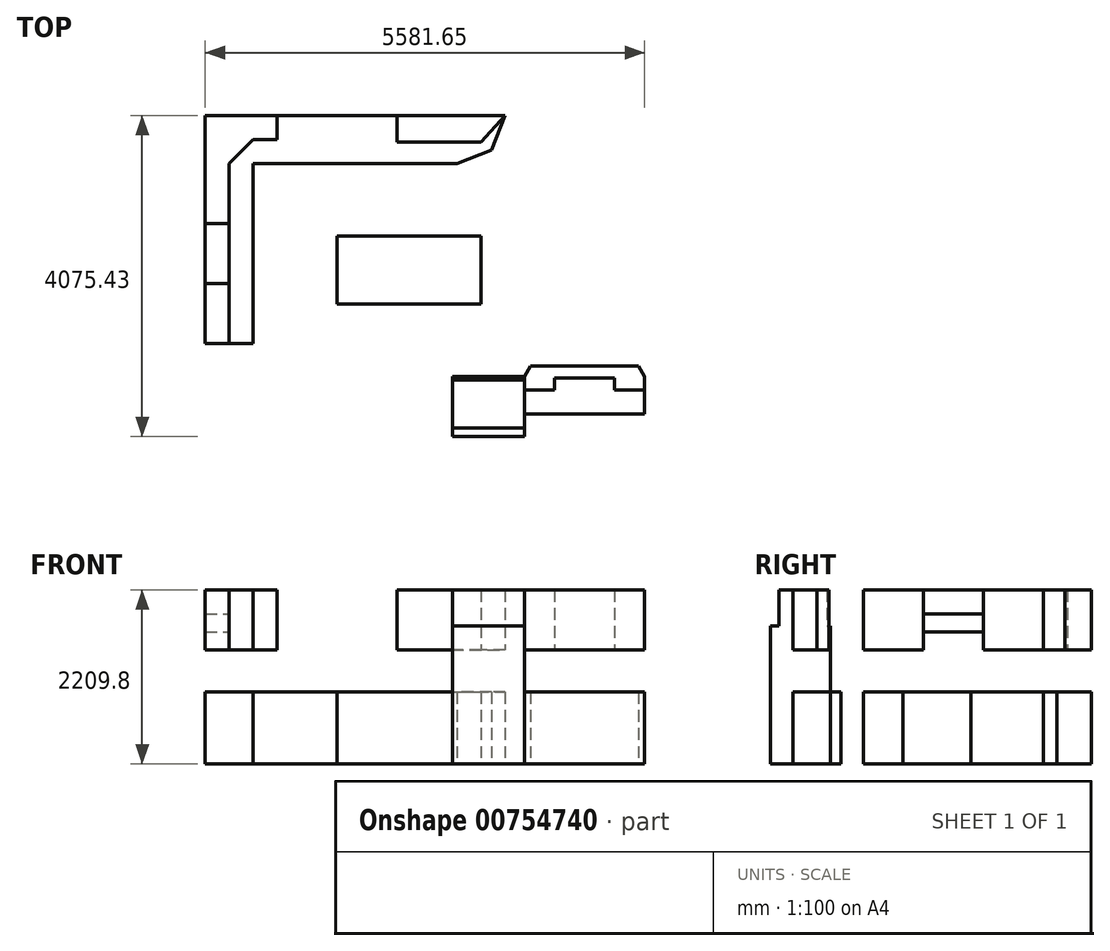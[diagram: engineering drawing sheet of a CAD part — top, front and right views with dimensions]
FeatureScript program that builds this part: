
annotation { "Feature Type Name" : "Feature", "Feature Type Description" : "" }
export const myFeature = defineFeature(function(context is Context, id is Id, definition is map)
    precondition{}
    {
        {
            var Q0;
            Q0=qCreatedBy(makeId("Top.planeOp"),FACE);
            cPlane(context, id + "F0", {"entities" : qUnion([Q0]), "cplaneType" : CPlaneType.OFFSET, "offset" : 1447.8 * mm, "width" : 152.4 * mm, "height" : 152.4 * mm});
        }
        {
            var Q0;
            Q0=qCreatedBy(makeId("Top.planeOp"),FACE);
            cPlane(context, id + "F1", {"entities" : qUnion([Q0]), "cplaneType" : CPlaneType.OFFSET, "offset" : 2286 * mm, "width" : 152.4 * mm, "height" : 152.4 * mm});
        }
        {
            var Q0;
            Q0=qCreatedBy(makeId("Top.planeOp"),FACE);
            var sketch = newSketch(context, id + "F2", { "sketchPlane" : qUnion([Q0])});
            skLineSegment(sketch, "E0", {"start": v(0, 0) * mm, "end": v(1009.65, 0) * mm});
            skLineSegment(sketch, "E1", {"start": v(1009.65, 0) * mm, "end": v(2343.15, 0) * mm, "construction": true});
            skLineSegment(sketch, "E2", {"start": v(2343.15, 0) * mm, "end": v(4025.9, 0) * mm});
            skLineSegment(sketch, "E3", {"start": v(4025.9, 0) * mm, "end": v(5886.45, 0) * mm, "construction": true});
            skLineSegment(sketch, "E4", {"start": v(5886.45, 0) * mm, "end": v(6648.45, 0) * mm});
            skLineSegment(sketch, "E5", {"start": v(6648.45, 0) * mm, "end": v(6648.45, -247.65) * mm});
            skLineSegment(sketch, "E6", {"start": v(6648.45, -247.65) * mm, "end": v(6648.45, -1917.7) * mm, "construction": true});
            skLineSegment(sketch, "E7", {"start": v(6648.45, -2889.25) * mm, "end": v(6648.45, -3790.95) * mm});
            skLineSegment(sketch, "E8", {"start": v(6648.45, -3790.95) * mm, "end": v(5734.05, -3790.95) * mm, "construction": true});
            skLineSegment(sketch, "E9", {"start": v(5734.05, -3790.95) * mm, "end": v(4019.55, -3790.95) * mm});
            skLineSegment(sketch, "E10", {"start": v(3028.95, -3790.95) * mm, "end": v(3028.95, -4095.75) * mm});
            skLineSegment(sketch, "E11", {"start": v(3028.95, -4095.75) * mm, "end": v(1784.35, -4095.75) * mm, "construction": true});
            skLineSegment(sketch, "E12", {"start": v(1784.35, -4095.75) * mm, "end": v(920.75, -4095.75) * mm});
            skLineSegment(sketch, "E13", {"start": v(920.75, -4095.75) * mm, "end": v(0, -4095.75) * mm, "construction": true});
            skLineSegment(sketch, "E14", {"start": v(0, -4095.75) * mm, "end": v(0, -3048) * mm, "construction": true});
            skLineSegment(sketch, "E15", {"start": v(0, -3048) * mm, "end": v(0, -2895.6) * mm});
            skLineSegment(sketch, "E16", {"start": v(0, -2895.6) * mm, "end": v(0, 0) * mm});
            skLineSegment(sketch, "E17", {"start": v(6648.45, -1917.7) * mm, "end": v(6648.45, -2889.25) * mm, "construction": true});
            skLineSegment(sketch, "E18", {"start": v(3943.35, -3905.25) * mm, "end": v(4057.65, -3905.25) * mm});
            skLineSegment(sketch, "E19", {"start": v(4057.65, -3905.25) * mm, "end": v(4057.65, -4184.65) * mm});
            skLineSegment(sketch, "E20", {"start": v(4057.65, -4184.65) * mm, "end": v(3143.25, -4184.65) * mm});
            skLineSegment(sketch, "E21", {"start": v(3143.25, -4184.65) * mm, "end": v(3143.25, -3905.25) * mm});
            skLineSegment(sketch, "E22", {"start": v(3143.25, -3905.25) * mm, "end": v(3257.55, -3905.25) * mm});
            skLineSegment(sketch, "E23", {"start": v(3257.55, -3905.25) * mm, "end": v(3257.55, -3790.95) * mm});
            skLineSegment(sketch, "E24", {"start": v(3257.55, -3790.95) * mm, "end": v(3028.95, -3790.95) * mm});
            skLineSegment(sketch, "E25", {"start": v(3943.35, -3905.25) * mm, "end": v(3943.35, -3790.95) * mm});
            skLineSegment(sketch, "E26", {"start": v(3943.35, -3790.95) * mm, "end": v(4019.55, -3790.95) * mm});
            skPoint(sketch, "E27", {"position": v(3143.25, -3790.95) * mm});
            skPoint(sketch, "E28", {"position": v(4057.65, -3790.95) * mm});
            skSolve(sketch);
        }
        {
            var Q0;
            Q0=qCreatedBy(makeId("Top.planeOp"),FACE);
            var sketch = newSketch(context, id + "F3", { "sketchPlane" : qUnion([Q0])});
            skLineSegment(sketch, "E29.bottom", {"start": v(0, -2895.6) * mm, "end": v(609.6, -2895.6) * mm});
            skLineSegment(sketch, "E29.top", {"start": v(0, -2133.6) * mm, "end": v(609.6, -2133.6) * mm});
            skLineSegment(sketch, "E29.left", {"start": v(0, -2895.6) * mm, "end": v(0, -2133.6) * mm});
            skLineSegment(sketch, "E29.right", {"start": v(609.6, -2895.6) * mm, "end": v(609.6, -2133.6) * mm});
            skLineSegment(sketch, "E30.top", {"start": v(0, -1371.6) * mm, "end": v(609.6, -1371.6) * mm});
            skLineSegment(sketch, "E30.left", {"start": v(0, -2133.6) * mm, "end": v(0, -1371.6) * mm});
            skLineSegment(sketch, "E30.right", {"start": v(609.6, -2133.6) * mm, "end": v(609.6, -1371.6) * mm});
            skLineSegment(sketch, "E31.top", {"start": v(0, -914.4) * mm, "end": v(609.6, -914.4) * mm});
            skLineSegment(sketch, "E31.left", {"start": v(0, -1371.6) * mm, "end": v(0, -914.4) * mm});
            skLineSegment(sketch, "E31.right", {"start": v(609.6, -1371.6) * mm, "end": v(609.6, -914.4) * mm});
            skLineSegment(sketch, "E32", {"start": v(609.6, -914.4) * mm, "end": v(609.6, -609.6) * mm});
            skLineSegment(sketch, "E33", {"start": v(609.6, -609.6) * mm, "end": v(914.4, -609.6) * mm});
            skLineSegment(sketch, "E34", {"start": v(914.4, -609.6) * mm, "end": v(914.4, 0) * mm});
            skLineSegment(sketch, "E35", {"start": v(914.4, 0) * mm, "end": v(0, 0) * mm});
            skLineSegment(sketch, "E36", {"start": v(0, 0) * mm, "end": v(0, -914.4) * mm});
            skLineSegment(sketch, "E37.bottom", {"start": v(1219.2, -609.6) * mm, "end": v(2133.6, -609.6) * mm});
            skLineSegment(sketch, "E37.top", {"start": v(1219.2, 0) * mm, "end": v(2133.6, 0) * mm});
            skLineSegment(sketch, "E37.left", {"start": v(1219.2, -609.6) * mm, "end": v(1219.2, 0) * mm});
            skLineSegment(sketch, "E37.right", {"start": v(2133.6, -609.6) * mm, "end": v(2133.6, 0) * mm});
            skPoint(sketch, "E38", {"position": v(1676.4, -609.6) * mm});
            skLineSegment(sketch, "E39.bottom", {"start": v(914.4, -609.6) * mm, "end": v(1219.2, -609.6) * mm});
            skLineSegment(sketch, "E39.top", {"start": v(914.4, 0) * mm, "end": v(1219.2, 0) * mm});
            skLineSegment(sketch, "E40.bottom", {"start": v(2133.6, -609.6) * mm, "end": v(2743.2, -609.6) * mm});
            skLineSegment(sketch, "E40.top", {"start": v(2133.6, 0) * mm, "end": v(2743.2, 0) * mm});
            skLineSegment(sketch, "E40.right", {"start": v(2743.2, -609.6) * mm, "end": v(2743.2, 0) * mm});
            skLineSegment(sketch, "E41.bottom", {"start": v(2743.2, -609.6) * mm, "end": v(3200.4, -609.6) * mm});
            skLineSegment(sketch, "E41.top", {"start": v(2743.2, 0) * mm, "end": v(3200.4, 0) * mm});
            skLineSegment(sketch, "E41.right", {"start": v(3200.4, -609.6) * mm, "end": v(3200.4, 0) * mm});
            skLineSegment(sketch, "E42", {"start": v(3200.4, 0) * mm, "end": v(3810, 0) * mm});
            skLineSegment(sketch, "E43", {"start": v(3810, 0) * mm, "end": v(3637.62, -437.22) * mm});
            skLineSegment(sketch, "E44", {"start": v(3637.62, -437.22) * mm, "end": v(3200.4, -609.6) * mm});
            skSolve(sketch);
        }
        {
            var Q0;
            Q0=qCreatedBy(id+"F0.planeOp",FACE);
            var sketch = newSketch(context, id + "F4", { "sketchPlane" : qUnion([Q0])});
            skLineSegment(sketch, "E45.bottom", {"start": v(0, -2895.6) * mm, "end": v(304.8, -2895.6) * mm});
            skLineSegment(sketch, "E45.top", {"start": v(0, -2133.6) * mm, "end": v(304.8, -2133.6) * mm});
            skLineSegment(sketch, "E45.left", {"start": v(0, -2895.6) * mm, "end": v(0, -2133.6) * mm});
            skLineSegment(sketch, "E45.right", {"start": v(304.8, -2895.6) * mm, "end": v(304.8, -2133.6) * mm});
            skLineSegment(sketch, "E46.top", {"start": v(0, -1371.6) * mm, "end": v(304.8, -1371.6) * mm});
            skLineSegment(sketch, "E47.top", {"start": v(0, -609.6) * mm, "end": v(304.8, -609.6) * mm});
            skLineSegment(sketch, "E47.left", {"start": v(0, -1371.6) * mm, "end": v(0, -609.6) * mm});
            skLineSegment(sketch, "E47.right", {"start": v(304.8, -1371.6) * mm, "end": v(304.8, -609.6) * mm});
            skLineSegment(sketch, "E48", {"start": v(0, -609.6) * mm, "end": v(0, 0) * mm});
            skLineSegment(sketch, "E49", {"start": v(0, 0) * mm, "end": v(609.6, 0) * mm});
            skLineSegment(sketch, "E50", {"start": v(609.6, 0) * mm, "end": v(609.6, -304.8) * mm});
            skLineSegment(sketch, "E51", {"start": v(609.6, -304.8) * mm, "end": v(304.8, -609.6) * mm});
            skLineSegment(sketch, "E52.bottom", {"start": v(609.6, 0) * mm, "end": v(914.4, 0) * mm});
            skLineSegment(sketch, "E52.top", {"start": v(609.6, -304.8) * mm, "end": v(914.4, -304.8) * mm});
            skLineSegment(sketch, "E52.right", {"start": v(914.4, 0) * mm, "end": v(914.4, -304.8) * mm});
            skLineSegment(sketch, "E53", {"start": v(3810, 0) * mm, "end": v(3505.2, -336.01) * mm});
            skLineSegment(sketch, "E54", {"start": v(3505.2, -336.01) * mm, "end": v(3505.2, 0) * mm});
            skLineSegment(sketch, "E55", {"start": v(3505.2, 0) * mm, "end": v(3810, 0) * mm});
            skLineSegment(sketch, "E56.bottom", {"start": v(3505.2, 0) * mm, "end": v(2743.2, 0) * mm});
            skLineSegment(sketch, "E56.top", {"start": v(3505.2, -339.07) * mm, "end": v(2743.2, -339.07) * mm});
            skLineSegment(sketch, "E56.left", {"start": v(3505.2, 0) * mm, "end": v(3505.2, -339.07) * mm});
            skLineSegment(sketch, "E56.right", {"start": v(2743.2, 0) * mm, "end": v(2743.2, -339.07) * mm});
            skLineSegment(sketch, "E57.bottom", {"start": v(2743.2, 0) * mm, "end": v(2438.4, 0) * mm});
            skLineSegment(sketch, "E57.top", {"start": v(2743.2, -339.07) * mm, "end": v(2438.4, -339.07) * mm});
            skLineSegment(sketch, "E57.right", {"start": v(2438.4, 0) * mm, "end": v(2438.4, -339.07) * mm});
            skSolve(sketch);
        }
        {
            var Q0;
            Q0=qCreatedBy(makeId("Top.planeOp"),FACE);
            var sketch = newSketch(context, id + "F5", { "sketchPlane" : qUnion([Q0])});
            skLineSegment(sketch, "E58.right", {"start": v(4057.65, -3313.33) * mm, "end": v(4057.65, -4075.33) * mm});
            skLineSegment(sketch, "E59.bottom", {"start": v(4133.85, -3790.95) * mm, "end": v(4819.65, -3790.95) * mm});
            skLineSegment(sketch, "E59.top", {"start": v(4133.85, -3181.35) * mm, "end": v(4819.65, -3181.35) * mm});
            skLineSegment(sketch, "E59.left", {"start": v(4133.85, -3790.95) * mm, "end": v(4133.85, -3181.35) * mm});
            skLineSegment(sketch, "E59.right", {"start": v(4819.65, -3790.95) * mm, "end": v(4819.65, -3181.35) * mm});
            skLineSegment(sketch, "E60.bottom", {"start": v(4819.65, -3181.35) * mm, "end": v(5505.45, -3181.35) * mm});
            skLineSegment(sketch, "E60.top", {"start": v(4819.65, -3790.95) * mm, "end": v(5505.45, -3790.95) * mm});
            skLineSegment(sketch, "E60.left", {"start": v(4819.65, -3181.35) * mm, "end": v(4819.65, -3790.95) * mm});
            skLineSegment(sketch, "E60.right", {"start": v(5505.45, -3181.35) * mm, "end": v(5505.45, -3790.95) * mm});
            skLineSegment(sketch, "E61", {"start": v(4133.85, -3181.35) * mm, "end": v(4057.65, -3313.33) * mm});
            skLineSegment(sketch, "E62", {"start": v(5505.45, -3181.35) * mm, "end": v(5581.65, -3313.33) * mm});
            skLineSegment(sketch, "E63", {"start": v(5581.65, -3313.33) * mm, "end": v(5581.65, -3790.95) * mm});
            skLineSegment(sketch, "E64", {"start": v(5581.65, -3790.95) * mm, "end": v(5505.45, -3790.95) * mm});
            skLineSegment(sketch, "E65", {"start": v(4133.85, -3790.95) * mm, "end": v(4057.65, -3790.95) * mm});
            skSolve(sketch);
        }
        {
            var Q0;
            Q0=qCreatedBy(id+"F0.planeOp",FACE);
            var sketch = newSketch(context, id + "F6", { "sketchPlane" : qUnion([Q0])});
            skLineSegment(sketch, "E66.bottom", {"start": v(4057.65, -3788.76) * mm, "end": v(4438.65, -3788.76) * mm});
            skLineSegment(sketch, "E66.top", {"start": v(4057.65, -3486.15) * mm, "end": v(4438.65, -3486.15) * mm});
            skLineSegment(sketch, "E66.left", {"start": v(4057.65, -3788.76) * mm, "end": v(4057.65, -3486.15) * mm});
            skLineSegment(sketch, "E66.right", {"start": v(4438.65, -3788.76) * mm, "end": v(4438.65, -3486.15) * mm});
            skLineSegment(sketch, "E67.bottom", {"start": v(4438.65, -3788.76) * mm, "end": v(5200.65, -3788.76) * mm});
            skLineSegment(sketch, "E67.top", {"start": v(4438.65, -3331.56) * mm, "end": v(5200.65, -3331.56) * mm});
            skLineSegment(sketch, "E67.left", {"start": v(4438.65, -3788.76) * mm, "end": v(4438.65, -3331.56) * mm});
            skLineSegment(sketch, "E67.right", {"start": v(5200.65, -3788.76) * mm, "end": v(5200.65, -3331.56) * mm});
            skLineSegment(sketch, "E68.bottom", {"start": v(5200.65, -3788.76) * mm, "end": v(5581.65, -3788.76) * mm});
            skLineSegment(sketch, "E68.top", {"start": v(5200.65, -3483.96) * mm, "end": v(5581.65, -3483.96) * mm});
            skLineSegment(sketch, "E68.left", {"start": v(5200.65, -3788.76) * mm, "end": v(5200.65, -3483.96) * mm});
            skLineSegment(sketch, "E68.right", {"start": v(5581.65, -3788.76) * mm, "end": v(5581.65, -3483.96) * mm});
            skSolve(sketch);
        }
        {
            var Q0;
            Q0=qCreatedBy(makeId("Top.planeOp"),FACE);
            var sketch = newSketch(context, id + "F7", { "sketchPlane" : qUnion([Q0])});
            skLineSegment(sketch, "E69.bottom", {"start": v(3143.23, -4075.43) * mm, "end": v(4057.63, -4075.43) * mm});
            skLineSegment(sketch, "E69.top", {"start": v(3143.23, -3313.43) * mm, "end": v(4057.63, -3313.43) * mm});
            skLineSegment(sketch, "E69.left", {"start": v(3143.23, -4075.43) * mm, "end": v(3143.23, -3313.43) * mm});
            skLineSegment(sketch, "E69.right", {"start": v(4057.63, -4075.43) * mm, "end": v(4057.63, -3313.43) * mm});
            skSolve(sketch);
        }
        {
            var Q0;
            Q0 = qSketchRegion(id + "F3", true);
            extrude(context, id + "F8", {"entities" : qUnion([Q0]), "depth" : 914.4 * mm, "offsetDistance" : 25.4 * mm});
        }
        {
            var Q0;
            {var subQ0=makeQuery(id+"F4.imprint","IMPRINT",EDGE,{"derivedFrom":sQuery(id+"F4.wireOp",EDGE,"E54")});var subQ1=makeQuery(id+"F4.imprint","IMPRINT",EDGE,{"derivedFrom":sQuery(id+"F4.wireOp",EDGE,"E56.right")});var subQ2=makeQuery(id+"F4.imprint","IMPRINT",EDGE,{"derivedFrom":sQuery(id+"F4.wireOp",EDGE,"E50")});var subQ3=makeQuery(id+"F4.imprint","IMPRINT",EDGE,{"derivedFrom":sQuery(id+"F4.wireOp",EDGE,"E47.top")});Q0=qUnion([makeQuery(id+"F4.imprint","IMPRINT",FACE,{"disambiguationData":[TD([[makeQuery(id+"F4.imprint","IMPRINT",EDGE,{"derivedFrom":sQuery(id+"F4.wireOp",EDGE,"E45.bottom")}),1.0]])]}),makeQuery(id+"F4.imprint","IMPRINT",FACE,{"disambiguationData":[TD([[makeQuery(id+"F4.imprint","IMPRINT",EDGE,{"derivedFrom":sQuery(id+"F4.wireOp",EDGE,"E46.top")}),1.0]])]}),makeQuery(id+"F4.imprint","IMPRINT",FACE,{"disambiguationData":[TD([[subQ2,1.0]])]}),makeQuery(id+"F4.imprint","IMPRINT",FACE,{"disambiguationData":[TD([[subQ3,1.0]])]}),makeQuery(id+"F4.imprint","IMPRINT",FACE,{"disambiguationData":[TD([[makeQuery(id+"F4.imprint","IMPRINT",EDGE,{"derivedFrom":sQuery(id+"F4.wireOp",EDGE,"E53")}),-1.0]])]}),makeQuery(id+"F4.imprint","IMPRINT",FACE,{"disambiguationData":[TD([[subQ1,-1.0]])]}),makeQuery(id+"F4.imprint","IMPRINT",FACE,{"disambiguationData":[TD([[subQ0,1.0]])]})]);}
            extrude(context, id + "F9", {"entities" : qUnion([Q0]), "operationType" : NewBodyOperationType.ADD, "depth" : 762 * mm, "offsetDistance" : 25.4 * mm});
        }
        {
            var Q0;
            Q0 = qSketchRegion(id + "F5", true);
            extrude(context, id + "F10", {"entities" : qUnion([Q0]), "depth" : 914.4 * mm, "offsetDistance" : 25.4 * mm});
        }
        {
            var Q0;
            Q0 = qSketchRegion(id + "F6", true);
            extrude(context, id + "F11", {"entities" : qUnion([Q0]), "depth" : 762 * mm, "offsetDistance" : 25.4 * mm});
        }
        {
            var Q0;
            Q0 = qSketchRegion(id + "F7", true);
            extrude(context, id + "F12", {"entities" : qUnion([Q0]), "depth" : 1752.6 * mm, "offsetDistance" : 25.4 * mm});
        }
        {
            var Q0;
            Q0=makeQuery(id+"F12.opExtrude","CAP_FACE",FACE,{"disambiguationData":[OSD([sQuery(id+"F7.wireOp",EDGE,"E69.bottom"),sQuery(id+"F7.wireOp",EDGE,"E69.top"),sQuery(id+"F7.wireOp",EDGE,"E69.left"),sQuery(id+"F7.wireOp",EDGE,"E69.right")])],"isStart":false});
            var sketch = newSketch(context, id + "F13", { "sketchPlane" : qUnion([Q0])});
            skLineSegment(sketch, "E70.bottom", {"start": v(3143.23, -3359.12) * mm, "end": v(4057.63, -3359.12) * mm});
            skLineSegment(sketch, "E70.top", {"start": v(3143.23, -3968.72) * mm, "end": v(4057.63, -3968.72) * mm});
            skLineSegment(sketch, "E70.left", {"start": v(3143.23, -3359.12) * mm, "end": v(3143.23, -3968.72) * mm});
            skLineSegment(sketch, "E70.right", {"start": v(4057.63, -3359.12) * mm, "end": v(4057.63, -3968.72) * mm});
            skSolve(sketch);
        }
        {
            var Q0;
            Q0=makeQuery(id+"F9.opExtrude","CAP_FACE",FACE,{"disambiguationData":[OSD([sQuery(id+"F4.wireOp",EDGE,"E45.bottom"),sQuery(id+"F4.wireOp",EDGE,"E45.top"),sQuery(id+"F4.wireOp",EDGE,"E45.left"),sQuery(id+"F4.wireOp",EDGE,"E45.right")])],"isStart":false});
            var sketch = newSketch(context, id + "F14", { "sketchPlane" : qUnion([Q0])});
            skLineSegment(sketch, "E71.bottom", {"start": v(0, -2133.6) * mm, "end": v(304.8, -2133.6) * mm});
            skLineSegment(sketch, "E71.top", {"start": v(0, -1371.6) * mm, "end": v(304.8, -1371.6) * mm});
            skLineSegment(sketch, "E71.left", {"start": v(0, -2133.6) * mm, "end": v(0, -1371.6) * mm});
            skLineSegment(sketch, "E71.right", {"start": v(304.8, -2133.6) * mm, "end": v(304.8, -1371.6) * mm});
            skSolve(sketch);
        }
        {
            var Q0;
            Q0 = qSketchRegion(id + "F13", true);
            extrude(context, id + "F15", {"entities" : qUnion([Q0]), "operationType" : NewBodyOperationType.ADD, "depth" : 457.2 * mm, "offsetDistance" : 25.4 * mm});
        }
        {
            var Q0;
            Q0 = qSketchRegion(id + "F14", true);
            extrude(context, id + "F16", {"entities" : qUnion([Q0]), "oppositeDirection" : true, "depth" : 304.8 * mm, "offsetDistance" : 25.4 * mm});
        }
        {
            var Q0;
            Q0=makeQuery(id+"F16.opExtrude","CAP_FACE",FACE,{"disambiguationData":[OSD([sQuery(id+"F14.wireOp",EDGE,"E71.bottom"),sQuery(id+"F14.wireOp",EDGE,"E71.top"),sQuery(id+"F14.wireOp",EDGE,"E71.left"),sQuery(id+"F14.wireOp",EDGE,"E71.right")])],"isStart":false});
            var sketch = newSketch(context, id + "F17", { "sketchPlane" : qUnion([Q0])});
            skLineSegment(sketch, "E72.bottom", {"start": v(0, 2133.6) * mm, "end": v(304.8, 2133.6) * mm});
            skLineSegment(sketch, "E72.top", {"start": v(0, 1371.6) * mm, "end": v(304.8, 1371.6) * mm});
            skLineSegment(sketch, "E72.left", {"start": v(0, 2133.6) * mm, "end": v(0, 1371.6) * mm});
            skLineSegment(sketch, "E72.right", {"start": v(304.8, 2133.6) * mm, "end": v(304.8, 1371.6) * mm});
            skSolve(sketch);
        }
        {
            var Q0;
            Q0 = qSketchRegion(id + "F17", true);
            extrude(context, id + "F18", {"entities" : qUnion([Q0]), "depth" : 228.6 * mm, "offsetDistance" : 25.4 * mm});
        }
        {
            var Q0;
            Q0=qCreatedBy(id+"F1.planeOp",FACE);
            var sketch = newSketch(context, id + "F19", { "sketchPlane" : qUnion([Q0])});
            skLineSegment(sketch, "E73.bottom", {"start": v(0, 343.7) * mm, "end": v(6648.45, 343.7) * mm});
            skLineSegment(sketch, "E73.top", {"start": v(0, -3790.95) * mm, "end": v(6648.45, -3790.95) * mm});
            skLineSegment(sketch, "E73.left", {"start": v(0, 343.7) * mm, "end": v(0, -3790.95) * mm});
            skLineSegment(sketch, "E73.right", {"start": v(6648.45, 343.7) * mm, "end": v(6648.45, -3790.95) * mm});
            skSolve(sketch);
        }
        {
            var Q0;
            Q0=qCreatedBy(makeId("Top.planeOp"),FACE);
            var sketch = newSketch(context, id + "F20", { "sketchPlane" : qUnion([Q0])});
            skLineSegment(sketch, "E74.bottom", {"start": v(1676.4, -1529.72) * mm, "end": v(3505.2, -1529.72) * mm});
            skLineSegment(sketch, "E74.top", {"start": v(1676.4, -2393.32) * mm, "end": v(3505.2, -2393.32) * mm});
            skLineSegment(sketch, "E74.left", {"start": v(1676.4, -1529.72) * mm, "end": v(1676.4, -2393.32) * mm});
            skLineSegment(sketch, "E74.right", {"start": v(3505.2, -1529.72) * mm, "end": v(3505.2, -2393.32) * mm});
            skLineSegment(sketch, "E75", {"start": v(3505.2, -2393.32) * mm, "end": v(3505.2, -3313.43) * mm, "construction": true});
            skLineSegment(sketch, "E76", {"start": v(3505.2, -1529.72) * mm, "end": v(3505.2, -609.6) * mm, "construction": true});
            skLineSegment(sketch, "E77", {"start": v(3505.2, -609.6) * mm, "end": v(3004.16, -609.6) * mm, "construction": true});
            skLineSegment(sketch, "E78", {"start": v(1676.4, -1529.72) * mm, "end": v(609.6, -1529.72) * mm, "construction": true});
            skSolve(sketch);
        }
        {
            var Q0;
            Q0 = qSketchRegion(id + "F20", true);
            extrude(context, id + "F21", {"entities" : qUnion([Q0]), "depth" : 914.4 * mm, "offsetDistance" : 25.4 * mm});
        }
    });
